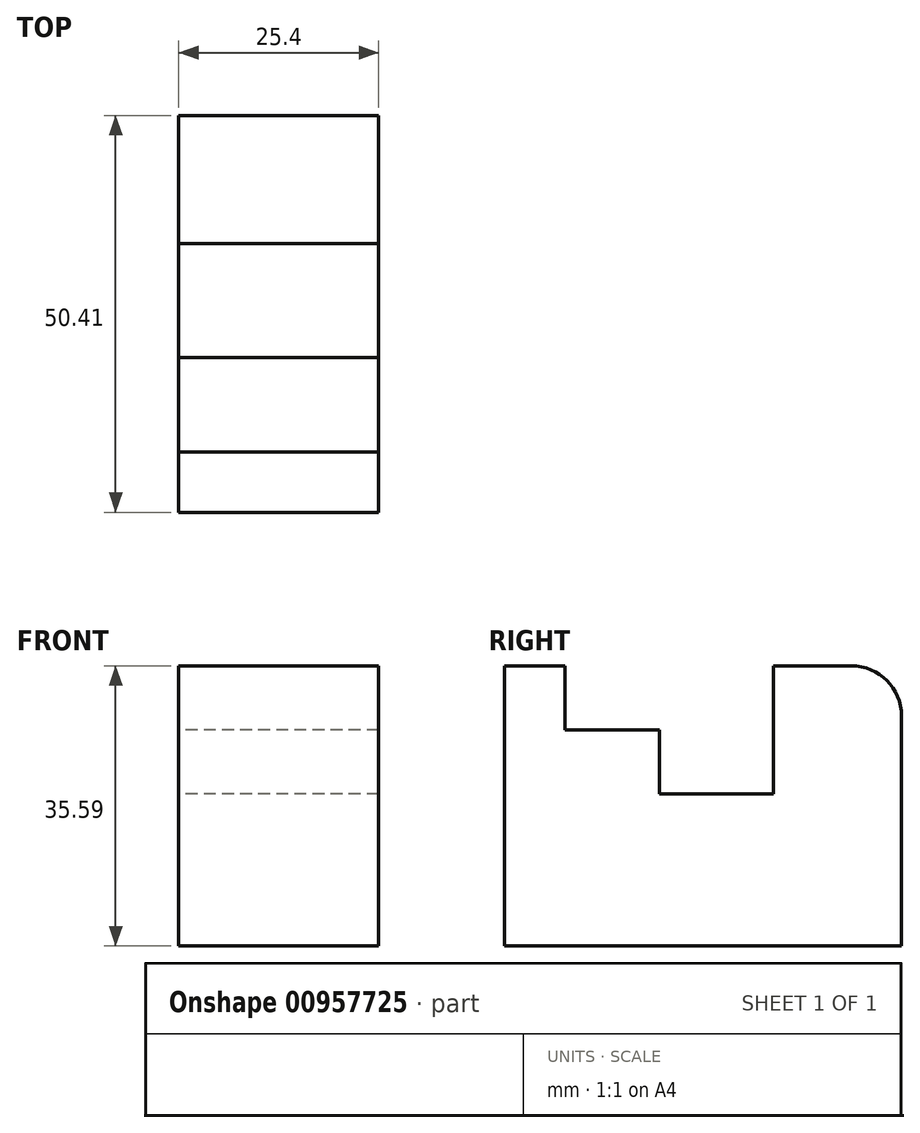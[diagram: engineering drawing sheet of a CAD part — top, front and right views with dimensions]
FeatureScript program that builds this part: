
annotation { "Feature Type Name" : "Feature", "Feature Type Description" : "" }
export const myFeature = defineFeature(function(context is Context, id is Id, definition is map)
    precondition{}
    {
        {
            var Q0;
            Q0=qCreatedBy(makeId("Right.planeOp"),FACE);
            var sketch = newSketch(context, id + "F0", { "sketchPlane" : qUnion([Q0])});
            skLineSegment(sketch, "E0", {"start": v(0, 0) * mm, "end": v(50.41, 0) * mm});
            skLineSegment(sketch, "E1", {"start": v(50.41, 0) * mm, "end": v(50.41, 29.24) * mm});
            skLineSegment(sketch, "E2", {"start": v(44.06, 35.59) * mm, "end": v(34.16, 35.59) * mm});
            skLineSegment(sketch, "E3", {"start": v(34.16, 35.59) * mm, "end": v(34.16, 19.33) * mm});
            skLineSegment(sketch, "E4", {"start": v(34.16, 19.33) * mm, "end": v(19.64, 19.33) * mm});
            skLineSegment(sketch, "E5", {"start": v(19.64, 19.33) * mm, "end": v(19.64, 27.46) * mm});
            skPoint(sketch, "E5.endSnap0", {"position": v(34.16, 27.46) * mm});
            skLineSegment(sketch, "E6", {"start": v(19.64, 27.46) * mm, "end": v(7.65, 27.46) * mm});
            skLineSegment(sketch, "E7", {"start": v(7.65, 27.46) * mm, "end": v(7.65, 35.59) * mm});
            skLineSegment(sketch, "E8", {"start": v(7.65, 35.59) * mm, "end": v(0, 35.59) * mm});
            skLineSegment(sketch, "E9", {"start": v(0, 35.59) * mm, "end": v(0, 0) * mm});
            skPoint(sketch, "E10.visualSharp", {"position": v(50.41, 35.59) * mm});
            skArc(sketch, "E10.filletArc", {"start": v(50.41, 29.24) * mm, "mid": v(48.55, 33.73) * mm, "end": v(44.06, 35.59) * mm});
            skSolve(sketch);
        }
        {
            var Q0;
            Q0 = qSketchRegion(id + "F0", true);
            extrude(context, id + "F1", {"entities" : qUnion([Q0]), "depth" : 25.4 * mm, "offsetDistance" : 25.4 * mm});
        }
    });
